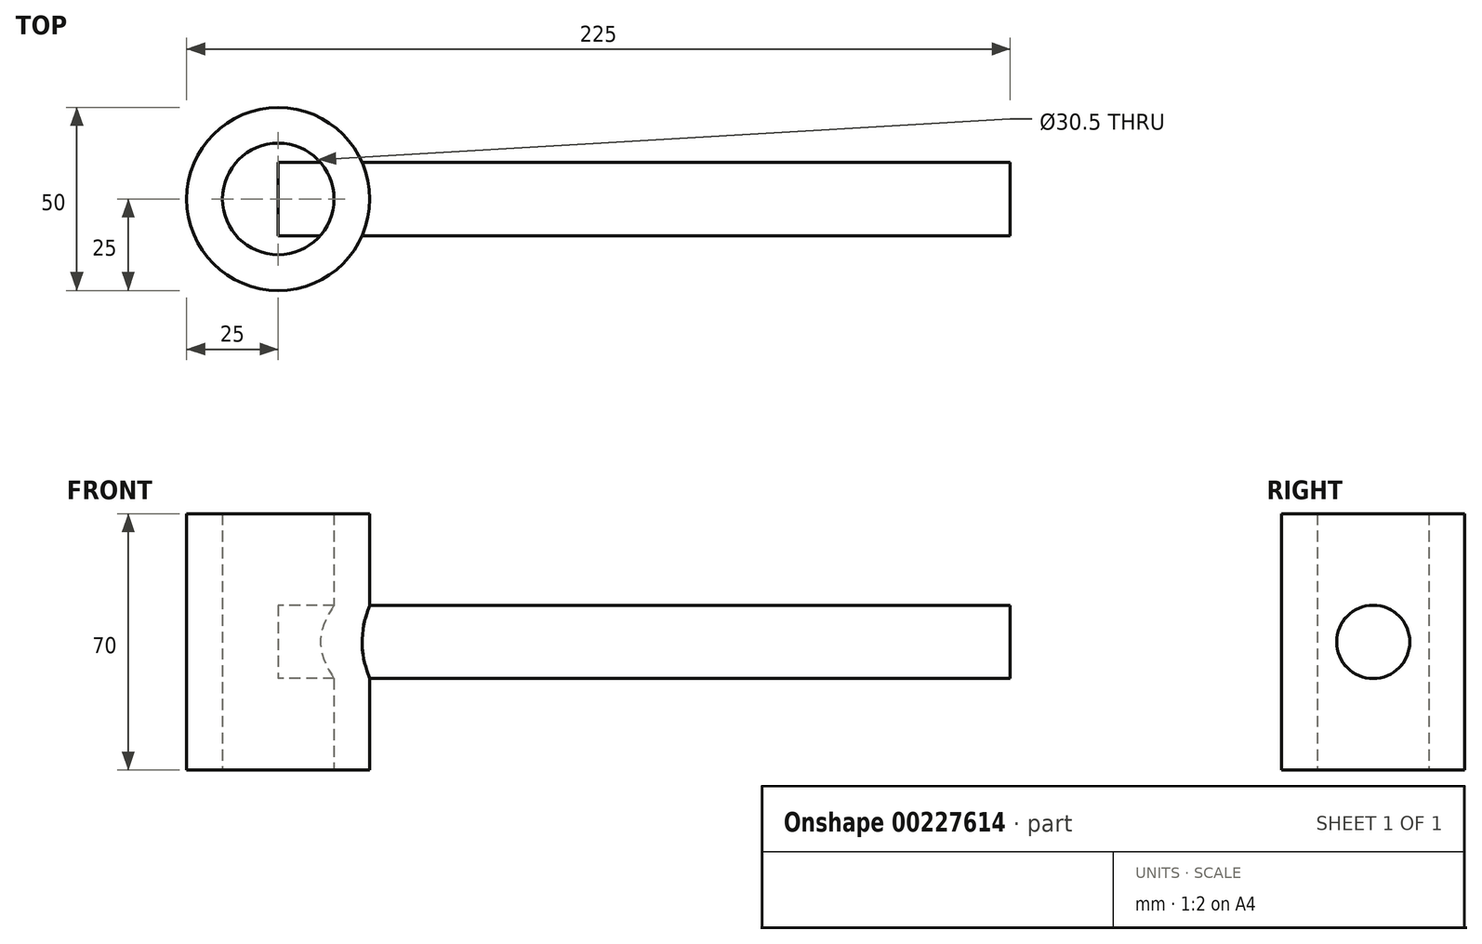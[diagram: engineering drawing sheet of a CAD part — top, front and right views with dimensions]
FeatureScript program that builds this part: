
annotation { "Feature Type Name" : "Feature", "Feature Type Description" : "" }
export const myFeature = defineFeature(function(context is Context, id is Id, definition is map)
    precondition{}
    {
        {
            var Q0;
            Q0=qCreatedBy(makeId("Top.planeOp"),FACE);
            var sketch = newSketch(context, id + "F0", { "sketchPlane" : qUnion([Q0])});
            skCircle(sketch, "E0", {"center": v(0, 0) * mm, "radius": 15.25 * mm});
            skCircle(sketch, "E1", {"center": v(0, 0) * mm, "radius": 25 * mm});
            skSolve(sketch);
        }
        {
            var Q0;
            Q0 = qSketchRegion(id + "F0", true);
            extrude(context, id + "F1", {"entities" : qUnion([Q0]), "endBound" : BoundingType.SYMMETRIC, "depth" : 70 * mm});
        }
        {
            var Q0;
            Q0=qCreatedBy(makeId("Right.planeOp"),FACE);
            var sketch = newSketch(context, id + "F2", { "sketchPlane" : qUnion([Q0])});
            skCircle(sketch, "E2", {"center": v(0, 0) * mm, "radius": 10 * mm});
            skSolve(sketch);
        }
        {
            var Q0;
            Q0 = qSketchRegion(id + "F2", true);
            extrude(context, id + "F3", {"entities" : qUnion([Q0]), "operationType" : NewBodyOperationType.ADD, "depth" : 200 * mm});
        }
    });
